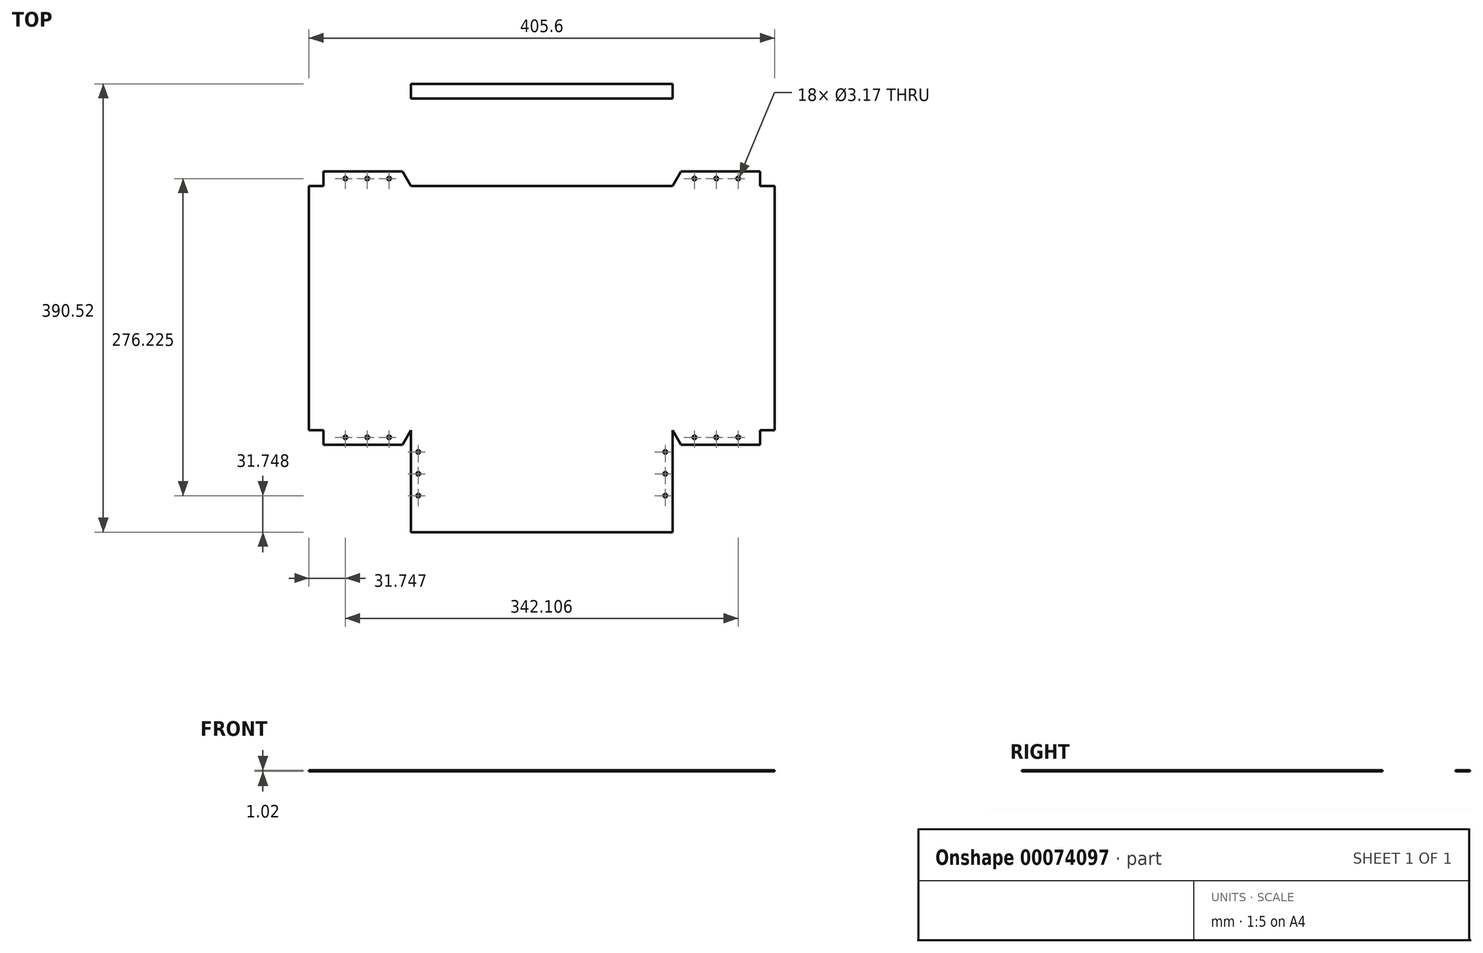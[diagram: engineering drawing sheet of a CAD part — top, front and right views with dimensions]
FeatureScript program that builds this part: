
annotation { "Feature Type Name" : "Feature", "Feature Type Description" : "" }
export const myFeature = defineFeature(function(context is Context, id is Id, definition is map)
    precondition{}
    {
        {
            var Q0;
            Q0=qCreatedBy(makeId("Top.planeOp"),FACE);
            var sketch = newSketch(context, id + "F0", { "sketchPlane" : qUnion([Q0])});
            skLineSegment(sketch, "E0.rect.bottom", {"start": v(113.9, 106.36) * mm, "end": v(-113.9, 106.36) * mm});
            skLineSegment(sketch, "E0.rect.top", {"start": v(113.9, -106.36) * mm, "end": v(-113.9, -106.36) * mm});
            skLineSegment(sketch, "E0.rect.left", {"start": v(113.9, 106.36) * mm, "end": v(113.9, -106.36) * mm});
            skLineSegment(sketch, "E0.rect.right", {"start": v(-113.9, 106.36) * mm, "end": v(-113.9, -106.36) * mm});
            skPoint(sketch, "E0.rect.middle", {"position": v(0, 0) * mm});
            skLineSegment(sketch, "E1.bottom", {"start": v(-113.9, 182.56) * mm, "end": v(113.9, 182.56) * mm});
            skLineSegment(sketch, "E1.top", {"start": v(-113.9, 106.36) * mm, "end": v(113.9, 106.36) * mm});
            skLineSegment(sketch, "E1.left", {"start": v(-113.9, 182.56) * mm, "end": v(-113.9, 106.36) * mm});
            skLineSegment(sketch, "E1.right", {"start": v(113.9, 182.56) * mm, "end": v(113.9, 106.36) * mm});
            skLineSegment(sketch, "E2.bottom", {"start": v(-113.9, 195.26) * mm, "end": v(113.9, 195.26) * mm});
            skLineSegment(sketch, "E2.left", {"start": v(-113.9, 195.26) * mm, "end": v(-113.9, 182.56) * mm});
            skLineSegment(sketch, "E2.right", {"start": v(113.9, 195.26) * mm, "end": v(113.9, 182.56) * mm});
            skLineSegment(sketch, "E3.MirrorCS", {"start": v(-113.9, -182.56) * mm, "end": v(113.9, -182.56) * mm});
            skLineSegment(sketch, "E4.MirrorCS", {"start": v(-113.9, -195.26) * mm, "end": v(-113.9, -182.56) * mm});
            skLineSegment(sketch, "E5.MirrorCS", {"start": v(-113.9, -195.26) * mm, "end": v(113.9, -195.26) * mm});
            skLineSegment(sketch, "E6.MirrorCS", {"start": v(113.9, -195.26) * mm, "end": v(113.9, -182.56) * mm});
            skLineSegment(sketch, "E7.MirrorCS", {"start": v(-113.9, -182.56) * mm, "end": v(-113.9, -106.36) * mm});
            skLineSegment(sketch, "E8.MirrorCS", {"start": v(113.9, -182.56) * mm, "end": v(113.9, -106.36) * mm});
            skLineSegment(sketch, "E9.bottom", {"start": v(-113.9, 106.36) * mm, "end": v(-107.55, 106.36) * mm});
            skLineSegment(sketch, "E9.top", {"start": v(-113.9, 182.56) * mm, "end": v(-107.55, 182.56) * mm});
            skLineSegment(sketch, "E9.left", {"start": v(-113.9, 106.36) * mm, "end": v(-113.9, 182.56) * mm});
            skLineSegment(sketch, "E10.bottom", {"start": v(-190.1, -106.36) * mm, "end": v(-113.9, -106.36) * mm});
            skLineSegment(sketch, "E10.top", {"start": v(-190.1, 106.36) * mm, "end": v(-113.9, 106.36) * mm});
            skLineSegment(sketch, "E10.left", {"start": v(-190.1, -106.36) * mm, "end": v(-190.1, 106.36) * mm});
            skLineSegment(sketch, "E10.right", {"start": v(-113.9, -106.36) * mm, "end": v(-113.9, 106.36) * mm});
            skLineSegment(sketch, "E11.bottom", {"start": v(-196.45, -106.36) * mm, "end": v(-190.1, -106.36) * mm});
            skLineSegment(sketch, "E11.top", {"start": v(-196.45, 106.36) * mm, "end": v(-190.1, 106.36) * mm});
            skLineSegment(sketch, "E11.left", {"start": v(-196.45, -106.36) * mm, "end": v(-196.45, 106.36) * mm});
            skLineSegment(sketch, "E12.bottom", {"start": v(-196.45, -106.36) * mm, "end": v(-202.8, -106.36) * mm});
            skLineSegment(sketch, "E12.top", {"start": v(-196.45, 106.36) * mm, "end": v(-202.8, 106.36) * mm});
            skLineSegment(sketch, "E12.right", {"start": v(-202.8, -106.36) * mm, "end": v(-202.8, 106.36) * mm});
            skLineSegment(sketch, "E13.bottom", {"start": v(-190.1, -119.06) * mm, "end": v(-113.9, -119.06) * mm});
            skLineSegment(sketch, "E13.left", {"start": v(-190.1, -119.06) * mm, "end": v(-190.1, -106.36) * mm});
            skLineSegment(sketch, "E13.right", {"start": v(-113.9, -119.06) * mm, "end": v(-113.9, -106.36) * mm});
            skLineSegment(sketch, "E14", {"start": v(-113.9, -106.36) * mm, "end": v(-121.24, -119.06) * mm});
            skLineSegment(sketch, "E15.MirrorCS", {"start": v(-190.1, 119.06) * mm, "end": v(-190.1, 106.36) * mm});
            skLineSegment(sketch, "E16.MirrorCS", {"start": v(-190.1, 119.06) * mm, "end": v(-113.9, 119.06) * mm});
            skLineSegment(sketch, "E17.MirrorCS", {"start": v(-113.9, 106.36) * mm, "end": v(-121.24, 119.06) * mm});
            skLineSegment(sketch, "E18", {"start": v(-113.9, 112.71) * mm, "end": v(-132.95, 112.71) * mm});
            skLineSegment(sketch, "E19", {"start": v(-171.05, 112.71) * mm, "end": v(-190.1, 112.71) * mm});
            skLineSegment(sketch, "E20", {"start": v(-171.05, 112.71) * mm, "end": v(-152, 112.71) * mm});
            skCircle(sketch, "E21", {"center": v(-171.05, 112.71) * mm, "radius": 1.59 * mm});
            skCircle(sketch, "E22", {"center": v(-152, 112.71) * mm, "radius": 1.59 * mm});
            skCircle(sketch, "E23", {"center": v(-132.95, 112.71) * mm, "radius": 1.59 * mm});
            skLineSegment(sketch, "E24", {"start": v(-107.55, 106.36) * mm, "end": v(-107.55, 125.41) * mm});
            skLineSegment(sketch, "E25", {"start": v(-107.55, 182.56) * mm, "end": v(-107.55, 163.51) * mm});
            skLineSegment(sketch, "E26", {"start": v(-107.55, 163.51) * mm, "end": v(-107.55, 144.46) * mm});
            skLineSegment(sketch, "E27", {"start": v(-152, 112.71) * mm, "end": v(-132.95, 112.71) * mm});
            skLineSegment(sketch, "E28", {"start": v(-107.55, 144.46) * mm, "end": v(-107.55, 125.41) * mm});
            skCircle(sketch, "E29", {"center": v(-107.55, 163.51) * mm, "radius": 1.59 * mm});
            skCircle(sketch, "E30", {"center": v(-107.55, 144.46) * mm, "radius": 1.59 * mm});
            skCircle(sketch, "E31", {"center": v(-107.55, 125.41) * mm, "radius": 1.59 * mm});
            skCircle(sketch, "E32.MirrorC", {"center": v(107.55, 125.41) * mm, "radius": 1.59 * mm});
            skCircle(sketch, "E33.MirrorC", {"center": v(107.55, 144.46) * mm, "radius": 1.59 * mm});
            skCircle(sketch, "E34.MirrorC", {"center": v(107.55, 163.51) * mm, "radius": 1.59 * mm});
            skCircle(sketch, "E35.MirrorC", {"center": v(-107.55, -125.41) * mm, "radius": 1.59 * mm});
            skCircle(sketch, "E36.MirrorC", {"center": v(-107.55, -144.46) * mm, "radius": 1.59 * mm});
            skCircle(sketch, "E37.MirrorC", {"center": v(-132.95, -112.71) * mm, "radius": 1.59 * mm});
            skCircle(sketch, "E38.MirrorC", {"center": v(-152, -112.71) * mm, "radius": 1.59 * mm});
            skCircle(sketch, "E39.MirrorC", {"center": v(-171.05, -112.71) * mm, "radius": 1.59 * mm});
            skCircle(sketch, "E40.MirrorC", {"center": v(-107.55, -163.51) * mm, "radius": 1.59 * mm});
            skCircle(sketch, "E41.MirrorC", {"center": v(107.55, -163.51) * mm, "radius": 1.59 * mm});
            skCircle(sketch, "E42.MirrorC", {"center": v(107.55, -144.46) * mm, "radius": 1.59 * mm});
            skCircle(sketch, "E43.MirrorC", {"center": v(107.55, -125.41) * mm, "radius": 1.59 * mm});
            skLineSegment(sketch, "E44.MirrorCS", {"start": v(196.45, -106.36) * mm, "end": v(190.1, -106.36) * mm});
            skLineSegment(sketch, "E45.MirrorCS", {"start": v(196.45, -106.36) * mm, "end": v(202.8, -106.36) * mm});
            skCircle(sketch, "E46.MirrorC", {"center": v(171.05, -112.71) * mm, "radius": 1.59 * mm});
            skCircle(sketch, "E47.MirrorC", {"center": v(132.95, -112.71) * mm, "radius": 1.59 * mm});
            skCircle(sketch, "E48.MirrorC", {"center": v(152, -112.71) * mm, "radius": 1.59 * mm});
            skLineSegment(sketch, "E49.MirrorCS", {"start": v(190.1, -119.06) * mm, "end": v(190.1, -106.36) * mm});
            skLineSegment(sketch, "E50.MirrorCS", {"start": v(190.1, -119.06) * mm, "end": v(113.9, -119.06) * mm});
            skLineSegment(sketch, "E51.MirrorCS", {"start": v(190.1, -106.36) * mm, "end": v(113.9, -106.36) * mm});
            skLineSegment(sketch, "E52.MirrorCS", {"start": v(113.9, -106.36) * mm, "end": v(121.24, -119.06) * mm});
            skLineSegment(sketch, "E53.MirrorCS", {"start": v(190.1, -106.36) * mm, "end": v(190.1, 106.36) * mm});
            skLineSegment(sketch, "E54.MirrorCS", {"start": v(196.45, -106.36) * mm, "end": v(196.45, 106.36) * mm});
            skLineSegment(sketch, "E55.MirrorCS", {"start": v(202.8, -106.36) * mm, "end": v(202.8, 106.36) * mm});
            skLineSegment(sketch, "E56.MirrorCS", {"start": v(196.45, 106.36) * mm, "end": v(202.8, 106.36) * mm});
            skLineSegment(sketch, "E57.MirrorCS", {"start": v(196.45, 106.36) * mm, "end": v(190.1, 106.36) * mm});
            skLineSegment(sketch, "E58.MirrorCS", {"start": v(190.1, 106.36) * mm, "end": v(113.9, 106.36) * mm});
            skLineSegment(sketch, "E59.MirrorCS", {"start": v(190.1, 119.06) * mm, "end": v(190.1, 106.36) * mm});
            skLineSegment(sketch, "E60.MirrorCS", {"start": v(190.1, 119.06) * mm, "end": v(113.9, 119.06) * mm});
            skLineSegment(sketch, "E61.MirrorCS", {"start": v(113.9, 106.36) * mm, "end": v(121.24, 119.06) * mm});
            skCircle(sketch, "E62.MirrorC", {"center": v(132.95, 112.71) * mm, "radius": 1.59 * mm});
            skCircle(sketch, "E63.MirrorC", {"center": v(152, 112.71) * mm, "radius": 1.59 * mm});
            skCircle(sketch, "E64.MirrorC", {"center": v(171.05, 112.71) * mm, "radius": 1.59 * mm});
            skSolve(sketch);
        }
        {
            var Q0;
            Q0=makeQuery(id+"F0.imprint","IMPRINT",FACE,{"disambiguationData":[TD([[makeQuery(id+"F0.imprint","IMPRINT",EDGE,{"derivedFrom":sQuery(id+"F0.wireOp",EDGE,"E4.MirrorCS")}),-1.0]])]});
            var Q1;
            Q1=makeQuery(id+"F0.imprint","IMPRINT",FACE,{"disambiguationData":[TD([[makeQuery(id+"F0.imprint","IMPRINT",EDGE,{"derivedFrom":sQuery(id+"F0.wireOp",EDGE,"E12.bottom")}),-1.0]])]});
            var Q2;
            Q2=makeQuery(id+"F0.imprint","IMPRINT",FACE,{"disambiguationData":[TD([[makeQuery(id+"F0.imprint","IMPRINT",EDGE,{"derivedFrom":sQuery(id+"F0.wireOp",EDGE,"E45.MirrorCS")}),1.0]])]});
            var Q3;
            Q3=makeQuery(id+"F0.imprint","IMPRINT",FACE,{"disambiguationData":[TD([[makeQuery(id+"F0.imprint","IMPRINT",EDGE,{"derivedFrom":sQuery(id+"F0.wireOp",EDGE,"E2.bottom")}),-1.0]])]});
            var Q4;
            Q4=makeQuery(id+"F0.imprint","IMPRINT",FACE,{"disambiguationData":[TD([[makeQuery(id+"F0.imprint","IMPRINT",EDGE,{"derivedFrom":sQuery(id+"F0.wireOp",EDGE,"E11.bottom")}),1.0]])]});
            var Q5;
            Q5=makeQuery(id+"F0.imprint","IMPRINT",FACE,{"disambiguationData":[TD([[makeQuery(id+"F0.imprint","IMPRINT",EDGE,{"derivedFrom":sQuery(id+"F0.wireOp",EDGE,"E44.MirrorCS")}),-1.0]])]});
            var Q6;
            Q6=makeQuery(id+"F0.imprint","IMPRINT",FACE,{"disambiguationData":[TD([[makeQuery(id+"F0.imprint","IMPRINT",EDGE,{"derivedFrom":sQuery(id+"F0.wireOp",EDGE,"E0.rect.left")}),1.0]])]});
            var Q7;
            Q7=makeQuery(id+"F0.imprint","IMPRINT",FACE,{"disambiguationData":[TD([[makeQuery(id+"F0.imprint","IMPRINT",EDGE,{"derivedFrom":sQuery(id+"F0.wireOp",EDGE,"E10.top")}),-1.0]])]});
            var Q8;
            Q8=makeQuery(id+"F0.imprint","IMPRINT",FACE,{"disambiguationData":[TD([[makeQuery(id+"F0.imprint","IMPRINT",EDGE,{"derivedFrom":sQuery(id+"F0.wireOp",EDGE,"E10.bottom")}),-1.0]])]});
            var Q9;
            {var subQ5=sQuery(id+"F0.wireOp",EDGE,"E16.MirrorCS");var subQ6=sQuery(id+"F0.wireOp",EDGE,"E15.MirrorCS");var subQ7=makeQuery(id+"F0.imprint","INTERSECT",VERTEX,{"derivedFrom":[subQ6,subQ5]});Q9=makeQuery(id+"F0.imprint","IMPRINT",FACE,{"disambiguationData":[TD([[makeQuery(id+"F0.imprint","IMPRINT",EDGE,{"disambiguationData":[TD([[subQ7,-1.0]])],"derivedFrom":subQ6}),1.0]])]});}
            var Q10;
            Q10=makeQuery(id+"F0.imprint","IMPRINT",FACE,{"disambiguationData":[TD([[makeQuery(id+"F0.imprint","IMPRINT",EDGE,{"derivedFrom":sQuery(id+"F0.wireOp",EDGE,"E46.MirrorC")}),-1.0]])]});
            var Q11;
            Q11=makeQuery(id+"F0.imprint","IMPRINT",FACE,{"disambiguationData":[TD([[makeQuery(id+"F0.imprint","IMPRINT",EDGE,{"derivedFrom":sQuery(id+"F0.wireOp",EDGE,"E58.MirrorCS")}),-1.0]])]});
            var Q12;
            {var subQ5=sQuery(id+"F0.wireOp",EDGE,"E10.top");Q12=makeQuery(id+"F0.imprint","IMPRINT",FACE,{"disambiguationData":[TD([[makeQuery(id+"F0.imprint","IMPRINT",EDGE,{"derivedFrom":subQ5}),1.0]])]});}
            var Q13;
            {var subQ11=sQuery(id+"F0.wireOp",EDGE,"E9.bottom");Q13=makeQuery(id+"F0.imprint","IMPRINT",FACE,{"disambiguationData":[TD([[makeQuery(id+"F0.imprint","IMPRINT",EDGE,{"derivedFrom":subQ11}),1.0]])]});}
            var Q14;
            {var subQ1=sQuery(id+"F0.wireOp",EDGE,"E0.rect.top");Q14=makeQuery(id+"F0.imprint","IMPRINT",FACE,{"disambiguationData":[TD([[makeQuery(id+"F0.imprint","IMPRINT",EDGE,{"derivedFrom":subQ1}),1.0]])]});}
            var Q15;
            {var subQ8=sQuery(id+"F0.wireOp",EDGE,"E1.top");Q15=makeQuery(id+"F0.imprint","IMPRINT",FACE,{"disambiguationData":[TD([[makeQuery(id+"F0.imprint","IMPRINT",EDGE,{"derivedFrom":subQ8}),1.0]])]});}
            var Q16;
            Q16=makeQuery(id+"F0.imprint","IMPRINT",FACE,{"disambiguationData":[TD([[makeQuery(id+"F0.imprint","IMPRINT",EDGE,{"derivedFrom":sQuery(id+"F0.wireOp",EDGE,"E0.rect.top")}),-1.0]])]});
            extrude(context, id + "F1", {"entities" : qUnion([Q0, Q1, Q2, Q3, Q4, Q5, Q6, Q7, Q8, Q9, Q10, Q11, Q12, Q13, Q14, Q15, Q16]), "endBound" : BoundingType.SYMMETRIC, "depth" : 1.02 * mm});
        }
    });
